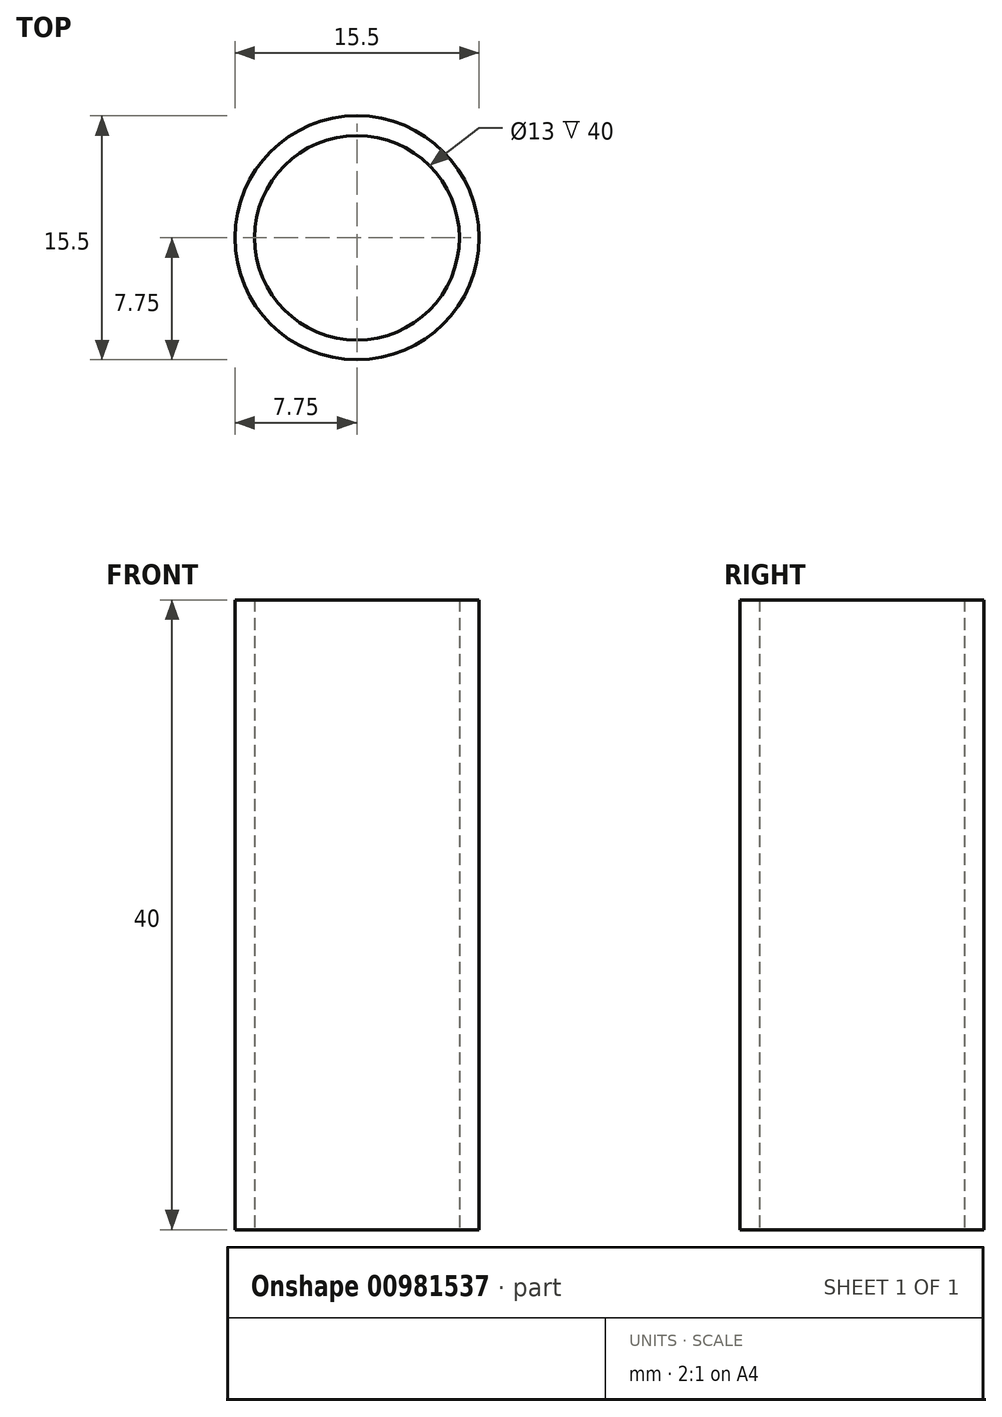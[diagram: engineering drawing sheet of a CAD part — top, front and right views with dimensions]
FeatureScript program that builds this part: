
annotation { "Feature Type Name" : "Feature", "Feature Type Description" : "" }
export const myFeature = defineFeature(function(context is Context, id is Id, definition is map)
    precondition{}
    {
        {
            var Q0;
            Q0=qCreatedBy(makeId("Top.planeOp"),FACE);
            var sketch = newSketch(context, id + "F0", { "sketchPlane" : qUnion([Q0])});
            skCircle(sketch, "E0", {"center": v(0, 0) * mm, "radius": 7.75 * mm});
            skCircle(sketch, "E1", {"center": v(0, 0) * mm, "radius": 6.5 * mm});
            skSolve(sketch);
        }
        {
            var Q0;
            Q0=makeQuery(id+"F0.imprint","IMPRINT",FACE,{"disambiguationData":[TD([[makeQuery(id+"F0.imprint","IMPRINT",EDGE,{"derivedFrom":sQuery(id+"F0.wireOp",EDGE,"E0")}),1.0]])]});
            extrude(context, id + "F1", {"entities" : qUnion([Q0]), "depth" : 40 * mm, "offsetDistance" : 25 * mm});
        }
    });
